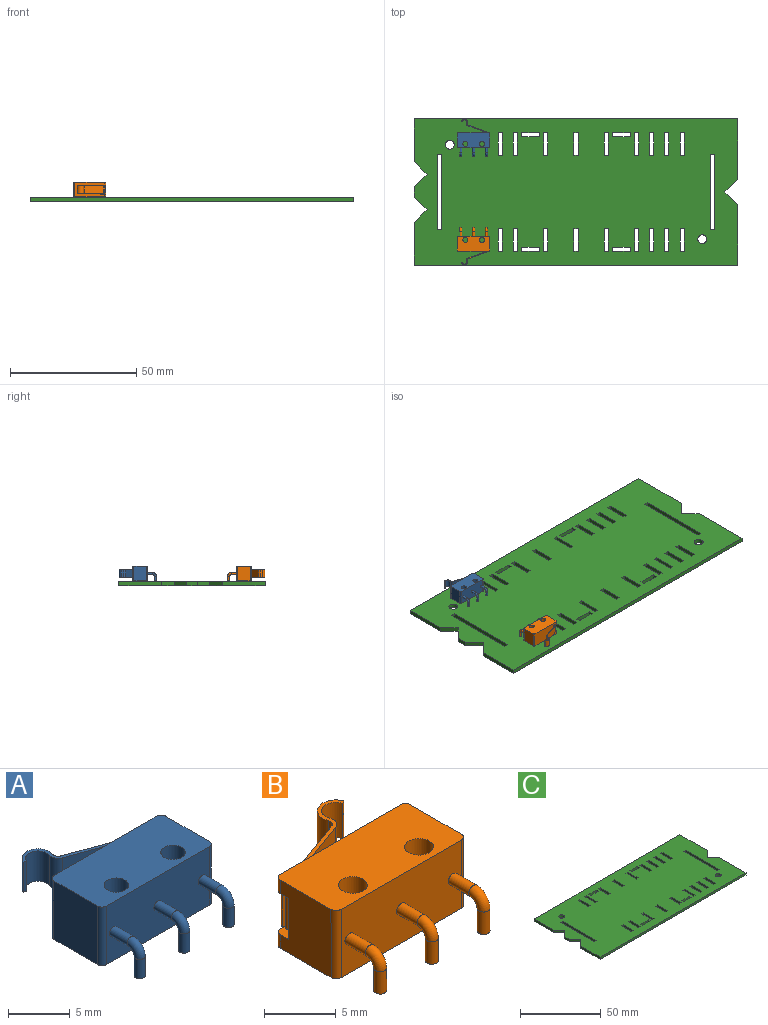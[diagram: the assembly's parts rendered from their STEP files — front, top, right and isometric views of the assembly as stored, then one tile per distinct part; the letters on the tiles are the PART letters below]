
ASSEMBLY  parts=3 mates=2
PART A: 42 faces, bbox 12.8x14.9x5.8 mm
  f0: cylinder r=0.45mm len=1.9mm, axis (0,0,-1), area 5.4mm2, adj f1,f2
  f1: plane 0.9x0.9mm, normal (0,0,-1), area 0.6mm2, adj f0
  f2: torus R=1mm, axis (1,0,0), area 4.4mm2, adj f0,f3
  f3: cylinder r=0.45mm len=2mm, axis (0,-1,0), area 5.7mm2, adj f2,f4
  f4: plane 11.8x5.8mm, normal (0,-1,0), area 66.5mm2, adj f3,f5,f6,f7,f8,f9,f10
  f5: cylinder r=0.5mm len=5.8mm, axis (0,0,1), area 4.6mm2, adj f4,f6,f8,f11
  f6: plane 12.8x6mm, normal (0,0,1), area 70.3mm2, adj f4,f5,f7,f11,f12,f13,f14,f15
  f7: cylinder r=0.5mm len=5.8mm, axis (0,0,1), area 4.6mm2, adj f4,f6,f8,f15
  f8: plane 12.8x6mm, normal (0,0,-1), area 70.3mm2, adj f4,f5,f7,f11,f13,f14,f15,f16
  f9: cylinder r=0.45mm len=2mm, axis (0,-1,0), area 5.7mm2, adj f4,f19
  f10: cylinder r=0.45mm len=2mm, axis (0,-1,0), area 5.7mm2, adj f4,f20
  f11: plane 5.8x5mm, normal (1,0,0), area 26.2mm2, adj f5,f6,f8,f12,f18,f21,f22,f23
  f12: cylinder r=0.5mm len=1.15mm, axis (0,0,-1), area 0.9mm2, adj f6,f11,f13,f21
  f13: plane 11.8x5.8mm, normal (0,1,0), area 63.2mm2, adj f6,f8,f12,f14,f18,f21,f22,f24
  f14: cylinder r=0.5mm len=5.8mm, axis (0,0,1), area 4.6mm2, adj f6,f8,f13,f15
  f15: plane 5.8x5mm, normal (-1,0,0), area 29mm2, adj f6,f7,f8,f14
  f16: cylinder r=1mm len=5.8mm, axis (0,0,1), area 36.4mm2, adj f6,f8
  f17: cylinder r=1mm len=5.8mm, axis (0,0,1), area 36.4mm2, adj f6,f8
  f18: cylinder r=0.5mm len=1.15mm, axis (0,0,-1), area 0.9mm2, adj f8,f11,f13,f22
  f19: torus R=1mm, axis (1,0,0), area 4.4mm2, adj f9,f25
  f20: torus R=1mm, axis (1,0,0), area 4.4mm2, adj f10,f26
  f21: plane 2x1.3mm, normal (0,0,-1), area 2.2mm2, adj f11,f12,f13,f23,f24,f27,f28
  f22: plane 2x1.3mm, normal (0,0,1), area 2.2mm2, adj f11,f13,f18,f23,f24,f27,f28
  f23: plane 3.5x1mm, normal (0,1,0), area 3.5mm2, adj f11,f21,f22,f27
  f24: plane 3.5x0.3mm, normal (1,0,0), area 1.1mm2, adj f13,f21,f22,f27
  f25: cylinder r=0.45mm len=1.9mm, axis (0,0,-1), area 5.4mm2, adj f19,f29
  f26: cylinder r=0.45mm len=1.9mm, axis (0,0,-1), area 5.4mm2, adj f20,f30
  f27: cylinder r=1mm len=3.5mm, axis (0,0,1), area 5.5mm2, adj f21,f22,f23,f24
  f28: cylinder r=0.2mm len=3.5mm, axis (0,0,1), area 3.8mm2, adj f21,f22,f31,f32,f33,f34
  f29: plane 0.9x0.9mm, normal (0,0,-1), area 0.6mm2, adj f25
  f30: plane 0.9x0.9mm, normal (0,0,-1), area 0.6mm2, adj f26
  f31: plane 7.71x3mm, normal (-0.34,-0.94,0), area 24.6mm2, adj f28,f32,f34,f35
  f32: plane 10.77x5.63mm, normal (0,0,1), area 4mm2, adj f28,f31,f33,f35,f36,f37,f38,f39
  f33: plane 3x0.3mm, normal (0.17,-0.98,0), area 0.9mm2, adj f28,f32,f34,f38
  f34: plane 10.77x5.63mm, normal (0,0,-1), area 4mm2, adj f28,f31,f33,f35,f36,f37,f38,f39
  f35: cylinder r=0.8mm len=3mm, axis (0,0,1), area 3.8mm2, adj f31,f32,f34,f41
  f36: plane 7.71x3mm, normal (0.34,0.94,0), area 24.6mm2, adj f32,f34,f37,f38
  f37: cylinder r=0.5mm len=3mm, axis (0,0,1), area 2.4mm2, adj f32,f34,f36,f39
  f38: cylinder r=0.5mm len=3mm, axis (0,0,1), area 1.6mm2, adj f32,f33,f34,f36
  f39: cylinder r=1.3mm len=3mm, axis (0,0,1), area 12.3mm2, adj f32,f34,f37,f40
  f40: plane 3x0.28mm, normal (-0.34,-0.94,0), area 0.9mm2, adj f32,f34,f39,f41
  f41: cylinder r=1mm len=3mm, axis (0,0,1), area 9.4mm2, adj f32,f34,f35,f40
PART B: 42 faces, bbox 12.8x14.9x5.8 mm
  f0: cylinder r=0.45mm len=1.9mm, axis (0,0,-1), area 5.4mm2, adj f1,f2
  f1: plane 0.9x0.9mm, normal (0,0,-1), area 0.6mm2, adj f0
  f2: torus R=1mm, axis (-1,0,0), area 4.4mm2, adj f0,f3
  f3: cylinder r=0.45mm len=2mm, axis (0,-1,0), area 5.7mm2, adj f2,f4
  f4: plane 11.8x5.8mm, normal (0,-1,0), area 66.5mm2, adj f3,f5,f6,f7,f8,f9,f10
  f5: cylinder r=0.5mm len=5.8mm, axis (0,0,1), area 4.6mm2, adj f4,f6,f8,f11
  f6: plane 12.8x6mm, normal (0,0,1), area 70.3mm2, adj f4,f5,f7,f11,f12,f13,f14,f15
  f7: cylinder r=0.5mm len=5.8mm, axis (0,0,1), area 4.6mm2, adj f4,f6,f8,f15
  f8: plane 12.8x6mm, normal (0,0,-1), area 70.3mm2, adj f4,f5,f7,f11,f13,f14,f15,f16
  f9: cylinder r=0.45mm len=2mm, axis (0,-1,0), area 5.7mm2, adj f4,f19
  f10: cylinder r=0.45mm len=2mm, axis (0,-1,0), area 5.7mm2, adj f4,f20
  f11: plane 5.81x5.01mm, normal (-1,0,0), area 26.2mm2, adj f5,f6,f8,f12,f18,f21,f22,f23
  f12: cylinder r=0.5mm len=1.15mm, axis (0,0,-1), area 0.9mm2, adj f6,f11,f13,f21
  f13: plane 11.8x5.8mm, normal (0,1,0), area 63.2mm2, adj f6,f8,f12,f14,f18,f21,f22,f24
  f14: cylinder r=0.5mm len=5.8mm, axis (0,0,1), area 4.6mm2, adj f6,f8,f13,f15
  f15: plane 5.81x5.01mm, normal (1,0,0), area 29mm2, adj f6,f7,f8,f14
  f16: cylinder r=1mm len=5.8mm, axis (0,0,1), area 36.4mm2, adj f6,f8
  f17: cylinder r=1mm len=5.8mm, axis (0,0,1), area 36.4mm2, adj f6,f8
  f18: cylinder r=0.5mm len=1.15mm, axis (0,0,-1), area 0.9mm2, adj f8,f11,f13,f22
  f19: torus R=1mm, axis (-1,0,0), area 4.4mm2, adj f9,f25
  f20: torus R=1mm, axis (-1,0,0), area 4.4mm2, adj f10,f26
  f21: plane 2x1.3mm, normal (0,0,-1), area 2.2mm2, adj f11,f12,f13,f23,f24,f27,f28
  f22: plane 2x1.3mm, normal (0,0,1), area 2.2mm2, adj f11,f13,f18,f23,f24,f27,f28
  f23: plane 3.5x1mm, normal (0,1,0), area 3.5mm2, adj f11,f21,f22,f27
  f24: plane 3.5x0.3mm, normal (-1,0,0), area 1.1mm2, adj f13,f21,f22,f27
  f25: cylinder r=0.45mm len=1.9mm, axis (0,0,-1), area 5.4mm2, adj f19,f29
  f26: cylinder r=0.45mm len=1.9mm, axis (0,0,-1), area 5.4mm2, adj f20,f30
  f27: cylinder r=1mm len=3.5mm, axis (0,0,1), area 5.5mm2, adj f21,f22,f23,f24
  f28: cylinder r=0.2mm len=3.5mm, axis (0,0,1), area 3.8mm2, adj f21,f22,f31,f32,f33,f34
  f29: plane 0.9x0.9mm, normal (0,0,-1), area 0.6mm2, adj f25
  f30: plane 0.9x0.9mm, normal (0,0,-1), area 0.6mm2, adj f26
  f31: plane 7.71x3mm, normal (0.34,-0.94,0), area 24.6mm2, adj f28,f32,f34,f35
  f32: plane 10.77x5.63mm, normal (0,0,1), area 4mm2, adj f28,f31,f33,f35,f36,f37,f38,f39
  f33: plane 3x0.3mm, normal (-0.17,-0.98,0), area 0.9mm2, adj f28,f32,f34,f38
  f34: plane 10.77x5.63mm, normal (0,0,-1), area 4mm2, adj f28,f31,f33,f35,f36,f37,f38,f39
  f35: cylinder r=0.8mm len=3mm, axis (0,0,1), area 3.8mm2, adj f31,f32,f34,f41
  f36: plane 7.71x3mm, normal (-0.34,0.94,0), area 24.6mm2, adj f32,f34,f37,f38
  f37: cylinder r=0.5mm len=3mm, axis (0,0,1), area 2.4mm2, adj f32,f34,f36,f39
  f38: cylinder r=0.5mm len=3mm, axis (0,0,1), area 1.6mm2, adj f32,f33,f34,f36
  f39: cylinder r=1.3mm len=3mm, axis (0,0,1), area 12.3mm2, adj f32,f34,f37,f40
  f40: plane 3x0.28mm, normal (0.34,-0.94,0), area 0.9mm2, adj f32,f34,f39,f41
  f41: cylinder r=1mm len=3mm, axis (0,0,1), area 9.4mm2, adj f32,f34,f35,f40
PART C: 113 faces, bbox 128x58x1.6 mm
  f0: plane 1.6x1.6mm, normal (0,-1,0), area 2.6mm2, adj f1,f110,f111,f112
  f1: plane 30x1.6mm, normal (-1,0,0), area 48mm2, adj f0,f2,f111,f112
  f2: plane 1.6x1.6mm, normal (0,1,0), area 2.6mm2, adj f1,f110,f111,f112
  f3: plane 1.6x1.6mm, normal (0,-1,0), area 2.6mm2, adj f4,f84,f111,f112
  f4: plane 30x1.6mm, normal (-1,0,0), area 48mm2, adj f3,f5,f111,f112
  f5: plane 1.6x1.6mm, normal (0,1,0), area 2.6mm2, adj f4,f84,f111,f112
  f6: plane 1.6x1.6mm, normal (0,-1,0), area 2.6mm2, adj f7,f85,f111,f112
  f7: plane 9x1.6mm, normal (-1,0,0), area 14.4mm2, adj f6,f8,f111,f112
  f8: plane 1.6x1.6mm, normal (0,1,0), area 2.6mm2, adj f7,f85,f111,f112
  f9: plane 7x1.6mm, normal (0,-1,0), area 11.2mm2, adj f10,f86,f111,f112
  f10: plane 1.6x1.6mm, normal (-1,0,0), area 2.6mm2, adj f9,f11,f111,f112
  f11: plane 7x1.6mm, normal (0,1,0), area 11.2mm2, adj f10,f86,f111,f112
  f12: plane 1.6x1.6mm, normal (0,1,0), area 2.6mm2, adj f13,f87,f111,f112
  f13: plane 9x1.6mm, normal (1,0,0), area 14.4mm2, adj f12,f14,f111,f112
  f14: plane 1.6x1.6mm, normal (0,-1,0), area 2.6mm2, adj f13,f87,f111,f112
  f15: plane 1.6x1.6mm, normal (0,1,0), area 2.6mm2, adj f16,f88,f111,f112
  f16: plane 9x1.6mm, normal (1,0,0), area 14.4mm2, adj f15,f17,f111,f112
  f17: plane 1.6x1.6mm, normal (0,-1,0), area 2.6mm2, adj f16,f88,f111,f112
  f18: plane 1.6x1.6mm, normal (0,1,0), area 2.6mm2, adj f19,f89,f111,f112
  f19: plane 9x1.6mm, normal (1,0,0), area 14.4mm2, adj f18,f20,f111,f112
  f20: plane 1.6x1.6mm, normal (0,-1,0), area 2.6mm2, adj f19,f89,f111,f112
  f21: plane 7x1.6mm, normal (0,-1,0), area 11.2mm2, adj f22,f90,f111,f112
  f22: plane 1.6x1.6mm, normal (-1,0,0), area 2.6mm2, adj f21,f23,f111,f112
  f23: plane 7x1.6mm, normal (0,1,0), area 11.2mm2, adj f22,f90,f111,f112
  f24: plane 1.6x1.6mm, normal (0,1,0), area 2.6mm2, adj f25,f91,f111,f112
  f25: plane 9x1.6mm, normal (1,0,0), area 14.4mm2, adj f24,f26,f111,f112
  f26: plane 1.6x1.6mm, normal (0,-1,0), area 2.6mm2, adj f25,f91,f111,f112
  f27: plane 1.6x1.6mm, normal (0,1,0), area 2.6mm2, adj f28,f92,f111,f112
  f28: plane 9x1.6mm, normal (1,0,0), area 14.4mm2, adj f27,f29,f111,f112
  f29: plane 1.6x1.6mm, normal (0,-1,0), area 2.6mm2, adj f28,f92,f111,f112
  f30: plane 5x5mm, normal (-0.71,0.71,0), area 11.3mm2, adj f31,f95,f111,f112
  f31: plane 17x1.6mm, normal (-1,0,0), area 27.2mm2, adj f30,f32,f111,f112
  f32: plane 128x1.6mm, normal (0,-1,0), area 204.8mm2, adj f31,f33,f111,f112
  f33: plane 24x1.6mm, normal (1,0,0), area 38.4mm2, adj f32,f34,f111,f112
  f34: plane 5x5mm, normal (0.71,0.71,0), area 11.3mm2, adj f33,f35,f111,f112
  f35: plane 5x5mm, normal (0.71,-0.71,0), area 11.3mm2, adj f34,f36,f111,f112
  f36: plane 24x1.6mm, normal (1,0,0), area 38.4mm2, adj f35,f37,f111,f112
  f37: plane 128x1.6mm, normal (0,1,0), area 204.8mm2, adj f36,f38,f111,f112
  f38: plane 17x1.6mm, normal (-1,0,0), area 27.2mm2, adj f37,f39,f111,f112
  f39: plane 5x5mm, normal (-0.71,-0.71,0), area 11.3mm2, adj f38,f40,f111,f112
  f40: plane 5x5mm, normal (-0.71,0.71,0), area 11.3mm2, adj f39,f41,f111,f112
  f41: plane 4x1.6mm, normal (-1,0,0), area 6.4mm2, adj f40,f95,f111,f112
  f42: plane 9x1.6mm, normal (1,0,0), area 14.4mm2, adj f43,f96,f111,f112
  f43: plane 1.6x1.6mm, normal (0,-1,0), area 2.6mm2, adj f42,f44,f111,f112
  f44: plane 9x1.6mm, normal (-1,0,0), area 14.4mm2, adj f43,f96,f111,f112
  f45: plane 9x1.6mm, normal (1,0,0), area 14.4mm2, adj f46,f97,f111,f112
  f46: plane 1.6x1.6mm, normal (0,-1,0), area 2.6mm2, adj f45,f47,f111,f112
  f47: plane 9x1.6mm, normal (-1,0,0), area 14.4mm2, adj f46,f97,f111,f112
  f48: plane 1.6x1.6mm, normal (1,0,0), area 2.6mm2, adj f49,f98,f111,f112
  f49: plane 7x1.6mm, normal (0,-1,0), area 11.2mm2, adj f48,f50,f111,f112
  f50: plane 1.6x1.6mm, normal (-1,0,0), area 2.6mm2, adj f49,f98,f111,f112
  f51: plane 1.6x1.6mm, normal (-1,0,0), area 2.6mm2, adj f52,f99,f111,f112
  f52: plane 7x1.6mm, normal (0,1,0), area 11.2mm2, adj f51,f53,f111,f112
  f53: plane 1.6x1.6mm, normal (1,0,0), area 2.6mm2, adj f52,f99,f111,f112
  f54: plane 1.6x1.6mm, normal (0,1,0), area 2.6mm2, adj f55,f100,f111,f112
  f55: plane 9x1.6mm, normal (1,0,0), area 14.4mm2, adj f54,f56,f111,f112
  f56: plane 1.6x1.6mm, normal (0,-1,0), area 2.6mm2, adj f55,f100,f111,f112
  f57: plane 9x1.6mm, normal (1,0,0), area 14.4mm2, adj f58,f101,f111,f112
  f58: plane 1.6x1.6mm, normal (0,-1,0), area 2.6mm2, adj f57,f59,f111,f112
  f59: plane 9x1.6mm, normal (-1,0,0), area 14.4mm2, adj f58,f101,f111,f112
  f60: plane 9x1.6mm, normal (1,0,0), area 14.4mm2, adj f61,f102,f111,f112
  f61: plane 1.6x1.6mm, normal (0,-1,0), area 2.6mm2, adj f60,f62,f111,f112
  f62: plane 9x1.6mm, normal (-1,0,0), area 14.4mm2, adj f61,f102,f111,f112
  f63: plane 9x1.6mm, normal (1,0,0), area 14.4mm2, adj f64,f103,f111,f112
  f64: plane 1.6x1.6mm, normal (0,-1,0), area 2.6mm2, adj f63,f65,f111,f112
  f65: plane 9x1.6mm, normal (-1,0,0), area 14.4mm2, adj f64,f103,f111,f112
  f66: plane 9x1.6mm, normal (1,0,0), area 14.4mm2, adj f67,f104,f111,f112
  f67: plane 1.6x1.6mm, normal (0,-1,0), area 2.6mm2, adj f66,f68,f111,f112
  f68: plane 9x1.6mm, normal (-1,0,0), area 14.4mm2, adj f67,f104,f111,f112
  f69: plane 9x1.6mm, normal (1,0,0), area 14.4mm2, adj f70,f105,f111,f112
  f70: plane 1.6x1.6mm, normal (0,-1,0), area 2.6mm2, adj f69,f71,f111,f112
  f71: plane 9x1.6mm, normal (-1,0,0), area 14.4mm2, adj f70,f105,f111,f112
  f72: plane 9x1.6mm, normal (1,0,0), area 14.4mm2, adj f73,f106,f111,f112
  f73: plane 1.6x1.6mm, normal (0,-1,0), area 2.6mm2, adj f72,f74,f111,f112
  f74: plane 9x1.6mm, normal (-1,0,0), area 14.4mm2, adj f73,f106,f111,f112
  f75: plane 9x1.6mm, normal (1,0,0), area 14.4mm2, adj f76,f107,f111,f112
  f76: plane 1.6x1.6mm, normal (0,-1,0), area 2.6mm2, adj f75,f77,f111,f112
  f77: plane 9x1.6mm, normal (-1,0,0), area 14.4mm2, adj f76,f107,f111,f112
  f78: plane 9x1.6mm, normal (1,0,0), area 14.4mm2, adj f79,f108,f111,f112
  f79: plane 1.6x1.6mm, normal (0,-1,0), area 2.6mm2, adj f78,f80,f111,f112
  f80: plane 9x1.6mm, normal (-1,0,0), area 14.4mm2, adj f79,f108,f111,f112
  f81: plane 9x1.6mm, normal (1,0,0), area 14.4mm2, adj f82,f109,f111,f112
  f82: plane 1.6x1.6mm, normal (0,-1,0), area 2.6mm2, adj f81,f83,f111,f112
  f83: plane 9x1.6mm, normal (-1,0,0), area 14.4mm2, adj f82,f109,f111,f112
  f84: plane 30x1.6mm, normal (1,0,0), area 48mm2, adj f3,f5,f111,f112
  f85: plane 9x1.6mm, normal (1,0,0), area 14.4mm2, adj f6,f8,f111,f112
  f86: plane 1.6x1.6mm, normal (1,0,0), area 2.6mm2, adj f9,f11,f111,f112
  f87: plane 9x1.6mm, normal (-1,0,0), area 14.4mm2, adj f12,f14,f111,f112
  f88: plane 9x1.6mm, normal (-1,0,0), area 14.4mm2, adj f15,f17,f111,f112
  f89: plane 9x1.6mm, normal (-1,0,0), area 14.4mm2, adj f18,f20,f111,f112
  f90: plane 1.6x1.6mm, normal (1,0,0), area 2.6mm2, adj f21,f23,f111,f112
  f91: plane 9x1.6mm, normal (-1,0,0), area 14.4mm2, adj f24,f26,f111,f112
  f92: plane 9x1.6mm, normal (-1,0,0), area 14.4mm2, adj f27,f29,f111,f112
  f93: cylinder r=1.75mm len=3.5mm, axis (0,0,-1), area 17.6mm2, adj f111,f112
  f94: cylinder r=1.75mm len=3.5mm, axis (0,0,-1), area 17.6mm2, adj f111,f112
  f95: plane 5x5mm, normal (-0.71,-0.71,0), area 11.3mm2, adj f30,f41,f111,f112
  f96: plane 1.6x1.6mm, normal (0,1,0), area 2.6mm2, adj f42,f44,f111,f112
  f97: plane 1.6x1.6mm, normal (0,1,0), area 2.6mm2, adj f45,f47,f111,f112
  f98: plane 7x1.6mm, normal (0,1,0), area 11.2mm2, adj f48,f50,f111,f112
  f99: plane 7x1.6mm, normal (0,-1,0), area 11.2mm2, adj f51,f53,f111,f112
  f100: plane 9x1.6mm, normal (-1,0,0), area 14.4mm2, adj f54,f56,f111,f112
  f101: plane 1.6x1.6mm, normal (0,1,0), area 2.6mm2, adj f57,f59,f111,f112
  f102: plane 1.6x1.6mm, normal (0,1,0), area 2.6mm2, adj f60,f62,f111,f112
  f103: plane 1.6x1.6mm, normal (0,1,0), area 2.6mm2, adj f63,f65,f111,f112
  f104: plane 1.6x1.6mm, normal (0,1,0), area 2.6mm2, adj f66,f68,f111,f112
  f105: plane 1.6x1.6mm, normal (0,1,0), area 2.6mm2, adj f69,f71,f111,f112
  f106: plane 1.6x1.6mm, normal (0,1,0), area 2.6mm2, adj f72,f74,f111,f112
  f107: plane 1.6x1.6mm, normal (0,1,0), area 2.6mm2, adj f75,f77,f111,f112
  f108: plane 1.6x1.6mm, normal (0,1,0), area 2.6mm2, adj f78,f80,f111,f112
  f109: plane 1.6x1.6mm, normal (0,1,0), area 2.6mm2, adj f81,f83,f111,f112
  f110: plane 30x1.6mm, normal (1,0,0), area 48mm2, adj f0,f2,f111,f112
  f111: plane 128x58mm, normal (0,0,1), area 6929.8mm2, adj f0,f1,f2,f3,f4,f5,f6,f7
  f112: plane 128x58mm, normal (0,0,-1), area 6929.8mm2, adj f0,f1,f2,f3,f4,f5,f6,f7
PLACE A t=(-30.73,16.4,-4.55)mm
PLACE B rot(axis=(0,0,-1),180deg) t=(-30.71,-12.61,-4.53)mm
PLACE C t=(9.85,1.92,-6.45)mm fixed
MATE fastened B.f13 <-> C.f109  axis (0,-1,0) through (-31.15,-21.58,-1.65)mm
MATE fastened A.f6 <-> B.f6  axis (0,0,1) through (-30.73,22.59,1.25)mm
